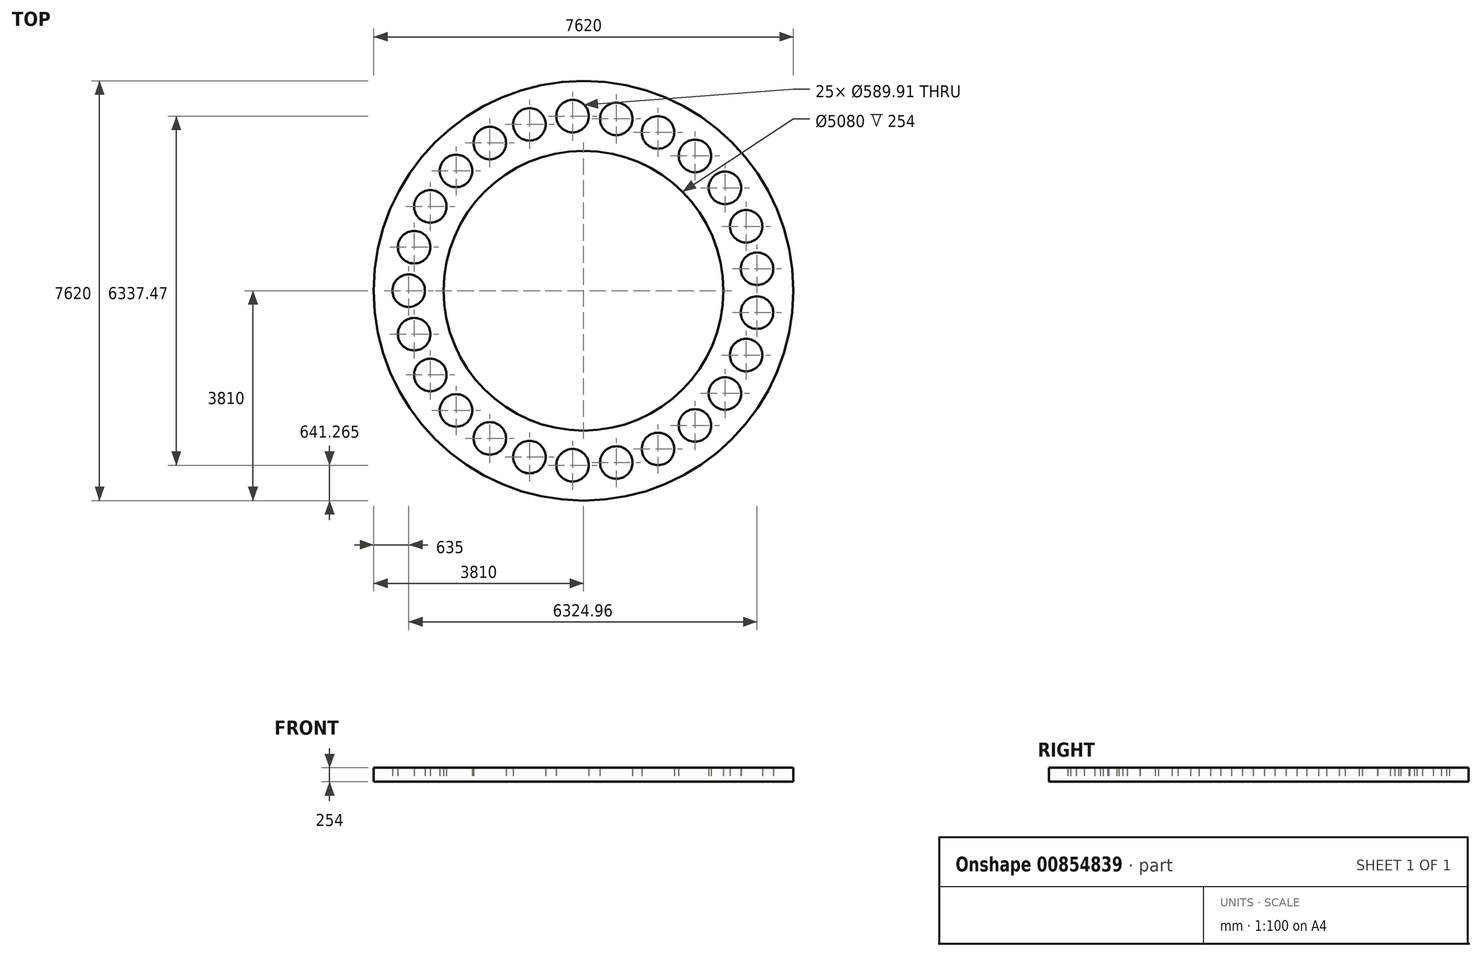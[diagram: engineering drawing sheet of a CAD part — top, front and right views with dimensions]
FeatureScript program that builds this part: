
annotation { "Feature Type Name" : "Feature", "Feature Type Description" : "" }
export const myFeature = defineFeature(function(context is Context, id is Id, definition is map)
    precondition{}
    {
        {
            var Q0;
            Q0=qCreatedBy(makeId("Top.planeOp"),FACE);
            var sketch = newSketch(context, id + "F0", { "sketchPlane" : qUnion([Q0])});
            skCircle(sketch, "E0", {"center": v(0, 0) * mm, "radius": 2540 * mm});
            skCircle(sketch, "E1", {"center": v(0, 0) * mm, "radius": 3175 * mm, "construction": true});
            skCircle(sketch, "E2", {"center": v(0, 0) * mm, "radius": 3810 * mm});
            skLineSegment(sketch, "E3", {"start": v(0, 0) * mm, "end": v(-4434.2, 0) * mm, "construction": true});
            skCircle(sketch, "E4", {"center": v(-3175, 0) * mm, "radius": 294.96 * mm});
            skCircle(sketch, "E5.1.0", {"center": v(-3075.25, -789.6) * mm, "radius": 294.96 * mm});
            skCircle(sketch, "E5.2.0", {"center": v(-2782.27, -1529.57) * mm, "radius": 294.96 * mm});
            skCircle(sketch, "E5.3.0", {"center": v(-2314.48, -2173.44) * mm, "radius": 294.96 * mm});
            skCircle(sketch, "E5.4.0", {"center": v(-1701.25, -2680.74) * mm, "radius": 294.96 * mm});
            skCircle(sketch, "E5.5.0", {"center": v(-981.13, -3019.6) * mm, "radius": 294.96 * mm});
            skCircle(sketch, "E5.6.0", {"center": v(-199.36, -3168.73) * mm, "radius": 294.96 * mm});
            skCircle(sketch, "E5.7.0", {"center": v(594.94, -3118.76) * mm, "radius": 294.96 * mm});
            skCircle(sketch, "E5.8.0", {"center": v(1351.85, -2872.83) * mm, "radius": 294.96 * mm});
            skCircle(sketch, "E5.9.0", {"center": v(2023.82, -2446.38) * mm, "radius": 294.96 * mm});
            skCircle(sketch, "E5.10.0", {"center": v(2568.63, -1866.22) * mm, "radius": 294.96 * mm});
            skCircle(sketch, "E5.11.0", {"center": v(2952.04, -1168.8) * mm, "radius": 294.96 * mm});
            skCircle(sketch, "E5.12.0", {"center": v(3149.96, -397.93) * mm, "radius": 294.96 * mm});
            skCircle(sketch, "E5.13.0", {"center": v(3149.96, 397.93) * mm, "radius": 294.96 * mm});
            skCircle(sketch, "E5.14.0", {"center": v(2952.04, 1168.8) * mm, "radius": 294.96 * mm});
            skCircle(sketch, "E5.15.0", {"center": v(2568.63, 1866.22) * mm, "radius": 294.96 * mm});
            skCircle(sketch, "E5.16.0", {"center": v(2023.82, 2446.38) * mm, "radius": 294.96 * mm});
            skCircle(sketch, "E5.17.0", {"center": v(1351.85, 2872.83) * mm, "radius": 294.96 * mm});
            skCircle(sketch, "E5.18.0", {"center": v(594.94, 3118.76) * mm, "radius": 294.96 * mm});
            skCircle(sketch, "E5.19.0", {"center": v(-199.36, 3168.73) * mm, "radius": 294.96 * mm});
            skCircle(sketch, "E5.20.0", {"center": v(-981.13, 3019.6) * mm, "radius": 294.96 * mm});
            skCircle(sketch, "E5.21.0", {"center": v(-1701.25, 2680.74) * mm, "radius": 294.96 * mm});
            skCircle(sketch, "E5.22.0", {"center": v(-2314.48, 2173.44) * mm, "radius": 294.96 * mm});
            skCircle(sketch, "E5.23.0", {"center": v(-2782.27, 1529.57) * mm, "radius": 294.96 * mm});
            skCircle(sketch, "E5.24.0", {"center": v(-3075.25, 789.6) * mm, "radius": 294.96 * mm});
            skSolve(sketch);
        }
        {
            var Q0;
            Q0=makeQuery(id+"F0.imprint","IMPRINT",FACE,{"disambiguationData":[TD([[makeQuery(id+"F0.imprint","IMPRINT",EDGE,{"derivedFrom":sQuery(id+"F0.wireOp",EDGE,"E0")}),-1.0]])]});
            var Q1;
            Q1=makeQuery(id+"F0.imprint","IMPRINT",FACE,{"disambiguationData":[TD([[makeQuery(id+"F0.imprint","IMPRINT",EDGE,{"derivedFrom":sQuery(id+"F0.wireOp",EDGE,"rZGO7bVd-L0fE-PMNe-PRq9-Aw8XqQe64tch")}),1.0]])]});
            extrude(context, id + "F1", {"entities" : qUnion([Q0, Q1]), "endBound" : BoundingType.SYMMETRIC, "depth" : 254 * mm, "offsetDistance" : 25.4 * mm});
        }
    });
